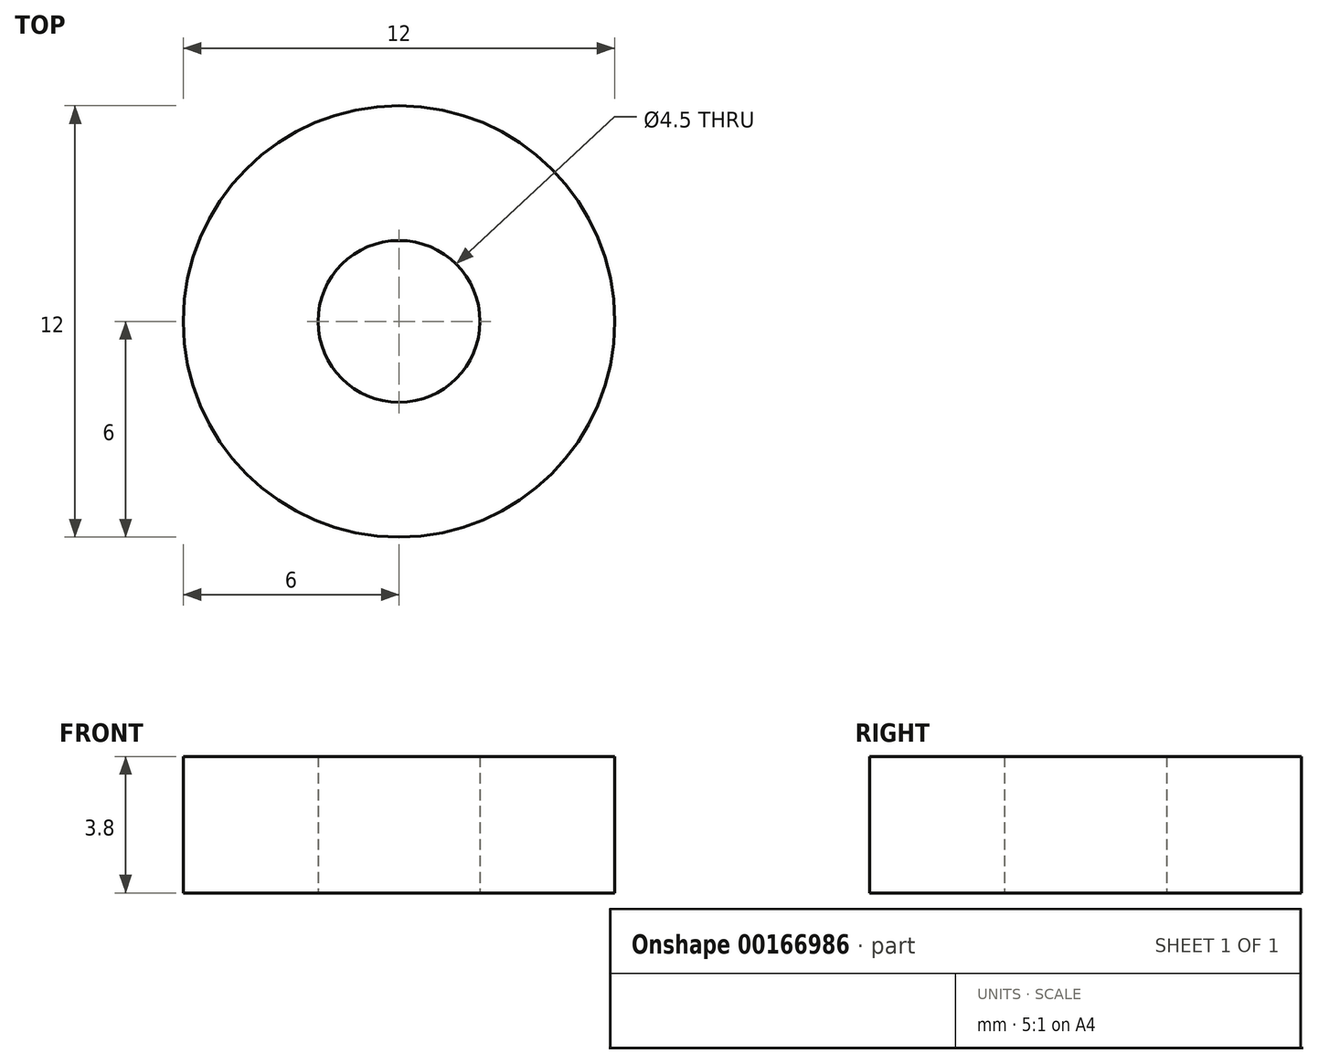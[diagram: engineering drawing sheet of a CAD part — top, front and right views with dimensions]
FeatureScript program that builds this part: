
annotation { "Feature Type Name" : "Feature", "Feature Type Description" : "" }
export const myFeature = defineFeature(function(context is Context, id is Id, definition is map)
    precondition{}
    {
        {
            var Q0;
            Q0=qCreatedBy(makeId("Top.planeOp"),FACE);
            var sketch = newSketch(context, id + "F0", { "sketchPlane" : qUnion([Q0])});
            skCircle(sketch, "E0", {"center": v(0, 0) * mm, "radius": 6 * mm});
            skCircle(sketch, "E1", {"center": v(0, 0) * mm, "radius": 2.25 * mm});
            skSolve(sketch);
        }
        {
            var Q0;
            Q0 = qSketchRegion(id + "F0", true);
            extrude(context, id + "F1", {"entities" : qUnion([Q0]), "depth" : 3.8 * mm});
        }
    });
